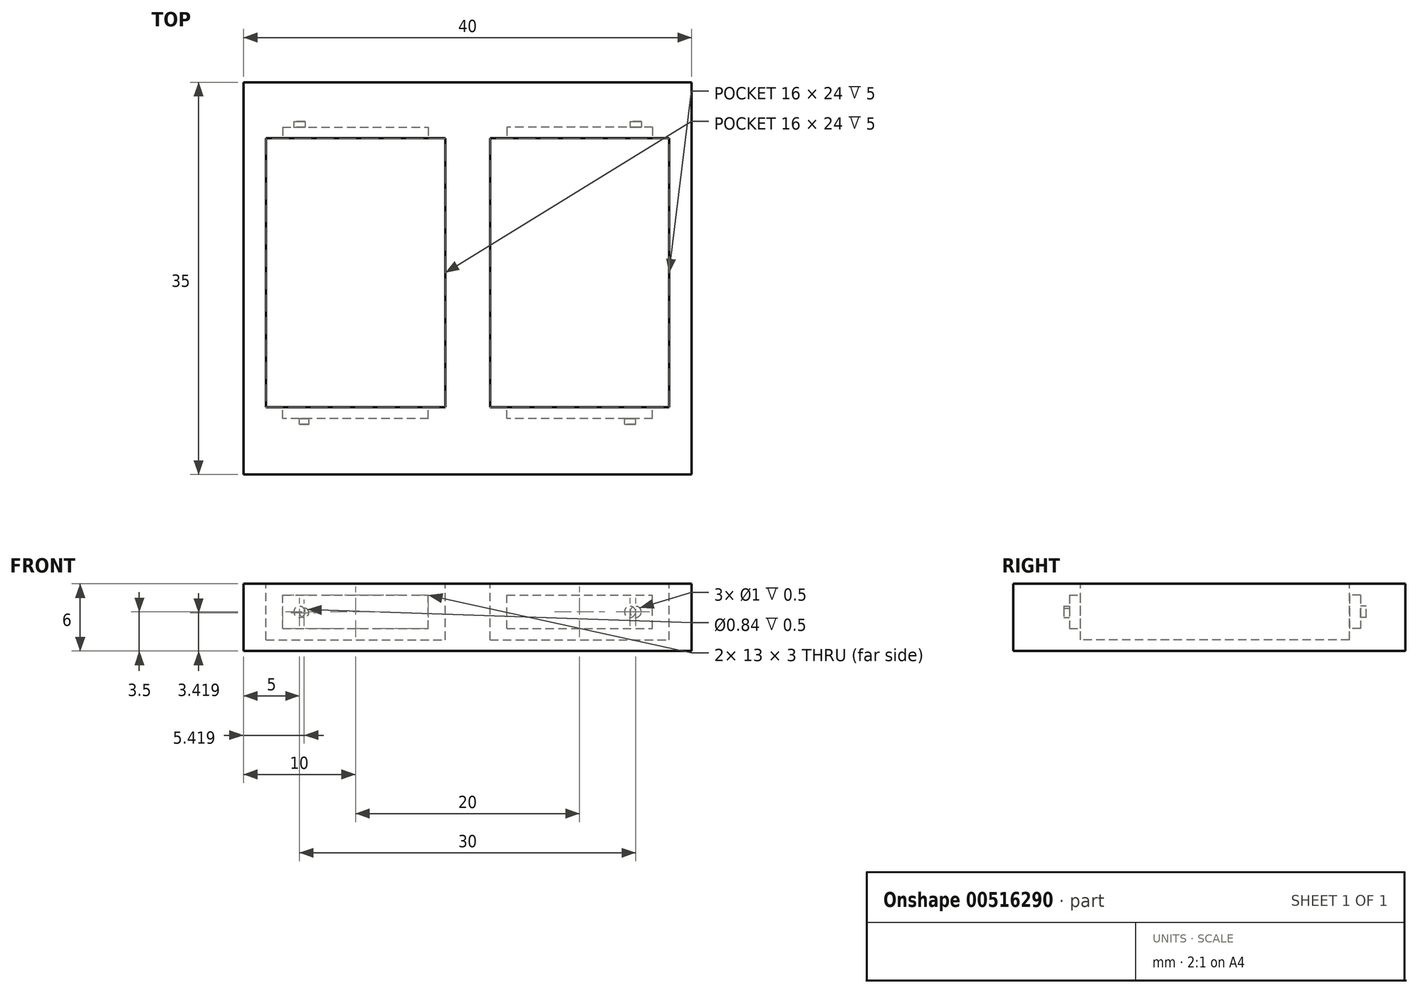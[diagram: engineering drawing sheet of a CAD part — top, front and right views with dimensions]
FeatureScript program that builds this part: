
annotation { "Feature Type Name" : "Feature", "Feature Type Description" : "" }
export const myFeature = defineFeature(function(context is Context, id is Id, definition is map)
    precondition{}
    {
        {
            var Q0;
            Q0=qCreatedBy(makeId("Top.planeOp"),FACE);
            var sketch = newSketch(context, id + "F0", { "sketchPlane" : qUnion([Q0])});
            skLineSegment(sketch, "E0.bottom", {"start": v(0, 0) * mm, "end": v(-40, 0) * mm});
            skLineSegment(sketch, "E0.top", {"start": v(0, 35) * mm, "end": v(-40, 35) * mm});
            skLineSegment(sketch, "E0.left", {"start": v(0, 0) * mm, "end": v(0, 35) * mm});
            skLineSegment(sketch, "E0.right", {"start": v(-40, 0) * mm, "end": v(-40, 35) * mm});
            skSolve(sketch);
        }
        {
            var Q0;
            Q0 = qSketchRegion(id + "F0", true);
            extrude(context, id + "F1", {"entities" : qUnion([Q0]), "depth" : 6 * mm, "offsetDistance" : 25 * mm});
        }
        {
            var Q0;
            Q0=makeQuery(id+"F1.opExtrude","CAP_FACE",FACE,{"disambiguationData":[OSD([sQuery(id+"F0.wireOp",EDGE,"E0.bottom"),sQuery(id+"F0.wireOp",EDGE,"E0.top"),sQuery(id+"F0.wireOp",EDGE,"E0.left"),sQuery(id+"F0.wireOp",EDGE,"E0.right")])],"isStart":false});
            var sketch = newSketch(context, id + "F2", { "sketchPlane" : qUnion([Q0])});
            skLineSegment(sketch, "E1", {"start": v(-20, 35) * mm, "end": v(-20, 0) * mm, "construction": true});
            skLineSegment(sketch, "E2.bottom", {"start": v(-38, 30) * mm, "end": v(-22, 30) * mm});
            skLineSegment(sketch, "E2.top", {"start": v(-38, 6) * mm, "end": v(-22, 6) * mm});
            skLineSegment(sketch, "E2.left", {"start": v(-38, 30) * mm, "end": v(-38, 6) * mm});
            skLineSegment(sketch, "E2.right", {"start": v(-22, 30) * mm, "end": v(-22, 6) * mm});
            skLineSegment(sketch, "E3.bottom", {"start": v(-18, 30) * mm, "end": v(-2, 30) * mm});
            skLineSegment(sketch, "E3.top", {"start": v(-18, 6) * mm, "end": v(-2, 6) * mm});
            skLineSegment(sketch, "E3.left", {"start": v(-18, 30) * mm, "end": v(-18, 6) * mm});
            skLineSegment(sketch, "E3.right", {"start": v(-2, 30) * mm, "end": v(-2, 6) * mm});
            skSolve(sketch);
        }
        {
            var Q0;
            Q0 = qSketchRegion(id + "F2", true);
            extrude(context, id + "F3", {"entities" : qUnion([Q0]), "operationType" : NewBodyOperationType.REMOVE, "oppositeDirection" : true, "depth" : 5 * mm, "offsetDistance" : 25 * mm});
        }
        {
            var Q0;
            Q0=makeQuery(id+"F3.boolean.opBoolean","COPY",FACE,{"derivedFrom":makeQuery(id+"F3.opExtrude","SWEPT_FACE",FACE,{"disambiguationData":[OSD([sQuery(id+"F2.wireOp",EDGE,"E2.bottom")])]})});
            var sketch = newSketch(context, id + "F4", { "sketchPlane" : qUnion([Q0])});
            skLineSegment(sketch, "E4.bottom", {"start": v(-36.5, 5) * mm, "end": v(-23.5, 5) * mm});
            skLineSegment(sketch, "E4.top", {"start": v(-36.5, 2) * mm, "end": v(-23.5, 2) * mm});
            skLineSegment(sketch, "E4.left", {"start": v(-36.5, 5) * mm, "end": v(-36.5, 2) * mm});
            skLineSegment(sketch, "E4.right", {"start": v(-23.5, 5) * mm, "end": v(-23.5, 2) * mm});
            skLineSegment(sketch, "E5.bottom", {"start": v(-3.5, 5) * mm, "end": v(-16.5, 5) * mm});
            skLineSegment(sketch, "E5.top", {"start": v(-3.5, 2) * mm, "end": v(-16.5, 2) * mm});
            skLineSegment(sketch, "E5.left", {"start": v(-3.5, 5) * mm, "end": v(-3.5, 2) * mm});
            skLineSegment(sketch, "E5.right", {"start": v(-16.5, 5) * mm, "end": v(-16.5, 2) * mm});
            skSolve(sketch);
        }
        {
            var Q0;
            Q0 = qSketchRegion(id + "F4", true);
            extrude(context, id + "F5", {"entities" : qUnion([Q0]), "operationType" : NewBodyOperationType.REMOVE, "oppositeDirection" : true, "depth" : 1 * mm, "offsetDistance" : 25 * mm, "hasSecondDirection" : true, "secondDirectionOppositeDirection" : false, "secondDirectionDepth" : 2 * mm});
        }
        {
            var Q0;
            Q0=makeQuery(id+"F5.boolean.opBoolean","COPY",FACE,{"derivedFrom":makeQuery(id+"F5.opExtrude","CAP_FACE",FACE,{"disambiguationData":[OSD([sQuery(id+"F4.wireOp",EDGE,"E4.bottom"),sQuery(id+"F4.wireOp",EDGE,"E4.top"),sQuery(id+"F4.wireOp",EDGE,"E4.left"),sQuery(id+"F4.wireOp",EDGE,"E4.right")])],"isStart":false})});
            var sketch = newSketch(context, id + "F6", { "sketchPlane" : qUnion([Q0])});
            skCircle(sketch, "E6", {"center": v(-35, 3.5) * mm, "radius": 0.5 * mm});
            skCircle(sketch, "E7", {"center": v(-5, 3.5) * mm, "radius": 0.5 * mm});
            skSolve(sketch);
        }
        {
            var Q0;
            Q0 = qSketchRegion(id + "F6", true);
            extrude(context, id + "F7", {"entities" : qUnion([Q0]), "operationType" : NewBodyOperationType.REMOVE, "oppositeDirection" : true, "depth" : 0.5 * mm, "offsetDistance" : 25 * mm});
        }
        {
            var Q0;
            Q0=makeQuery(id+"F3.boolean.opBoolean","COPY",FACE,{"derivedFrom":makeQuery(id+"F3.opExtrude","SWEPT_FACE",FACE,{"disambiguationData":[OSD([sQuery(id+"F2.wireOp",EDGE,"E3.top")])]})});
            var sketch = newSketch(context, id + "F8", { "sketchPlane" : qUnion([Q0])});
            skLineSegment(sketch, "E8.bottom", {"start": v(3.5, 5) * mm, "end": v(16.5, 5) * mm});
            skLineSegment(sketch, "E8.top", {"start": v(3.5, 2) * mm, "end": v(16.5, 2) * mm});
            skLineSegment(sketch, "E8.left", {"start": v(3.5, 5) * mm, "end": v(3.5, 2) * mm});
            skLineSegment(sketch, "E8.right", {"start": v(16.5, 5) * mm, "end": v(16.5, 2) * mm});
            skLineSegment(sketch, "E9.bottom", {"start": v(23.5, 5) * mm, "end": v(36.5, 5) * mm});
            skLineSegment(sketch, "E9.top", {"start": v(23.5, 2) * mm, "end": v(36.5, 2) * mm});
            skLineSegment(sketch, "E9.left", {"start": v(23.5, 5) * mm, "end": v(23.5, 2) * mm});
            skLineSegment(sketch, "E9.right", {"start": v(36.5, 5) * mm, "end": v(36.5, 2) * mm});
            skSolve(sketch);
        }
        {
            var Q0;
            Q0 = qSketchRegion(id + "F8", true);
            extrude(context, id + "F9", {"entities" : qUnion([Q0]), "operationType" : NewBodyOperationType.REMOVE, "oppositeDirection" : true, "depth" : 1 * mm, "offsetDistance" : 25 * mm, "hasSecondDirection" : true, "secondDirectionOppositeDirection" : false, "secondDirectionDepth" : 1 * mm});
        }
        {
            var Q0;
            Q0=makeQuery(id+"F9.boolean.opBoolean","COPY",FACE,{"derivedFrom":makeQuery(id+"F9.opExtrude","CAP_FACE",FACE,{"disambiguationData":[OSD([sQuery(id+"F8.wireOp",EDGE,"E8.bottom"),sQuery(id+"F8.wireOp",EDGE,"E8.top"),sQuery(id+"F8.wireOp",EDGE,"E8.left"),sQuery(id+"F8.wireOp",EDGE,"E8.right")])],"isStart":false})});
            var sketch = newSketch(context, id + "F10", { "sketchPlane" : qUnion([Q0])});
            skCircle(sketch, "E10", {"center": v(5.5, 3.5) * mm, "radius": 0.5 * mm});
            skPoint(sketch, "E10.centerSnap0", {"position": v(3.5, 3.5) * mm});
            skCircle(sketch, "E11", {"center": v(34.58, 3.42) * mm, "radius": 0.42 * mm});
            skSolve(sketch);
        }
        {
            var Q0;
            Q0 = qSketchRegion(id + "F10", true);
            extrude(context, id + "F11", {"entities" : qUnion([Q0]), "operationType" : NewBodyOperationType.REMOVE, "oppositeDirection" : true, "depth" : 0.5 * mm, "offsetDistance" : 25 * mm});
        }
    });
